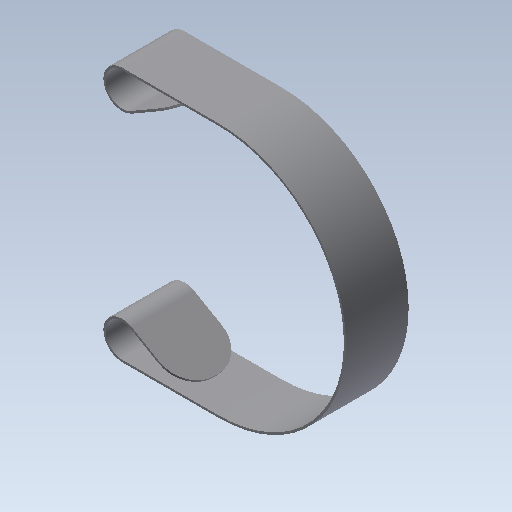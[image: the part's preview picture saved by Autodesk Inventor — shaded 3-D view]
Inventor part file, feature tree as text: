
AUTODESK INVENTOR PART (.ipt)
format: ipt  version: 2020.2 (Build 242310000, 310)  size: 289,792 bytes
history: native  units: mm
features: other x8, sketch x5, plane x2, hole x2
ambient origin geometry x8: Origin, YZ Plane, XZ Plane, XY Plane, X Axis, Y Axis, Z Axis, Center Point
bodies: Volumenkörper1 (feature_tree)
feature tree (17):
  other  "Fläche1"
  other  "Falten1"
  plane  "Arbeitsebene1"
  other  "Falz1"
  other  "Falz2"
  plane  "Arbeitsebene3"
  hole  "Bohrung2"  [1 undecoded]
  other  "Eckenrundung1"
  other  "Eckenrundung2"
  sketch  "Skizze1"  dims[d0=150.0mm d1=15.0mm]
  other  "Grobblech1"
  sketch  "Skizze3"  dims[d2=0.5mm d12=0.5mm]
  sketch  "Skizze10"  dims[d15=0.5mm d16=180.0deg d17=30.0mm d36=0.5mm d37=0.25mm d38=1.0mm d39=0.5mm d40=210.0deg d41=4.0mm d42=4.0mm d43=0.5mm d44=0.25mm d45=1.0mm d46=0.5mm d47=210.0deg d48=4.0mm d49=4.0mm d55=26.0mm d56=26.0mm d58=7.5mm d59=7.5mm d60=4.5mm d61=6.0mm d62=4.0mm d63=2.0mm d64=90.0deg d65=0.5mm d66=20.594885mm d67=7.0mm d68=7.0mm d69=0.5mm d3=22.5mm d4=4.2mm d5=6.0mm d6=4.0mm d7=2.0mm d8=90.0deg d9=8.0mm d10=20.594885mm]
  sketch  "Skizze7"  dims[d13=0.25mm]
  sketch  "Skizze8"  dims[d14=1.0mm]
  other  "Definition1"
  hole  "Bohrung1"  [1 undecoded]
note: 2 required parameter values undecoded (feature->parameter linkage not recoverable at this tier; creation-order binding heuristic only, values carry confidence <= 0.55)
